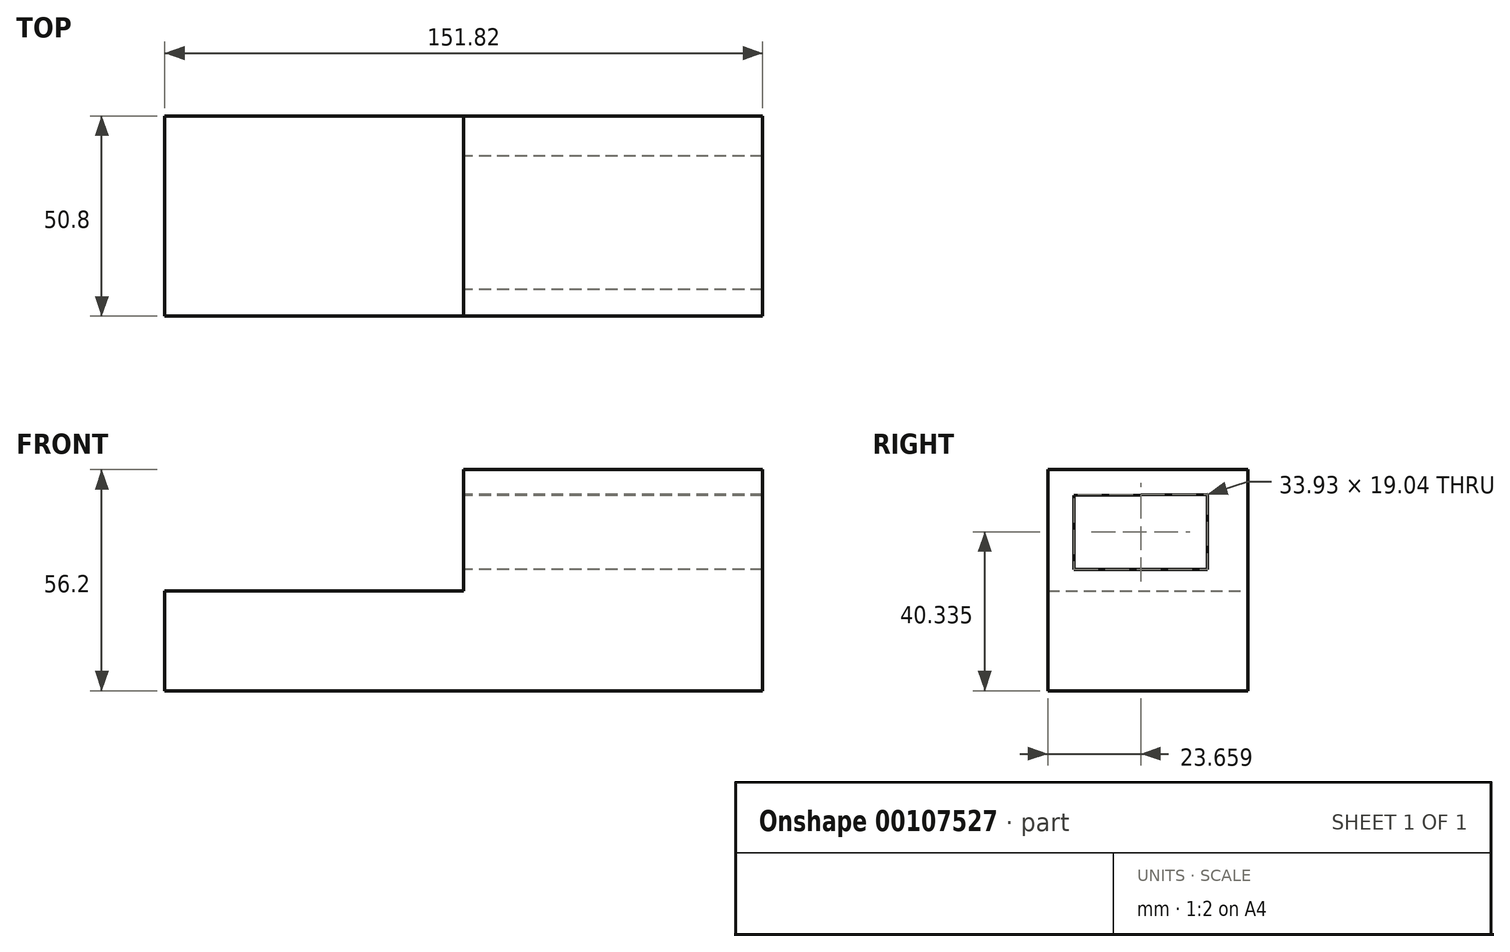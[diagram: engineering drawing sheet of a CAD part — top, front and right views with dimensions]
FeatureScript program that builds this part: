
annotation { "Feature Type Name" : "Feature", "Feature Type Description" : "" }
export const myFeature = defineFeature(function(context is Context, id is Id, definition is map)
    precondition{}
    {
        {
            var Q0;
            Q0=qCreatedBy(makeId("Front.planeOp"),FACE);
            var sketch = newSketch(context, id + "F0", { "sketchPlane" : qUnion([Q0])});
            skLineSegment(sketch, "E0", {"start": v(0, 56.2) * mm, "end": v(75.91, 56.2) * mm});
            skLineSegment(sketch, "E1", {"start": v(75.91, 56.2) * mm, "end": v(75.91, 0) * mm});
            skLineSegment(sketch, "E2", {"start": v(75.91, 0) * mm, "end": v(-75.91, 0) * mm});
            skLineSegment(sketch, "E3", {"start": v(-75.91, 0) * mm, "end": v(-75.91, 25.4) * mm});
            skLineSegment(sketch, "E4", {"start": v(-75.91, 25.4) * mm, "end": v(0, 25.4) * mm});
            skLineSegment(sketch, "E5", {"start": v(0, 25.4) * mm, "end": v(0, 56.2) * mm});
            skSolve(sketch);
        }
        {
            var Q0;
            Q0=makeQuery(id+"F0.imprint","IMPRINT",FACE,{"disambiguationData":[TD([[makeQuery(id+"F0.imprint","IMPRINT",EDGE,{"derivedFrom":sQuery(id+"F0.wireOp",EDGE,"E0")}),-1.0]])]});
            extrude(context, id + "F1", {"entities" : qUnion([Q0]), "depth" : 50.8 * mm});
        }
        {
            var Q0;
            Q0=qCreatedBy(makeId("Right.planeOp"),FACE);
            var sketch = newSketch(context, id + "F2", { "sketchPlane" : qUnion([Q0])});
            skLineSegment(sketch, "E6", {"start": v(-10.18, 49.85) * mm, "end": v(-10.18, 30.82) * mm});
            skLineSegment(sketch, "E7", {"start": v(-10.18, 30.82) * mm, "end": v(-44.1, 30.82) * mm});
            skLineSegment(sketch, "E8", {"start": v(-44.1, 30.82) * mm, "end": v(-44.1, 49.66) * mm});
            skLineSegment(sketch, "E9", {"start": v(-10.18, 49.85) * mm, "end": v(-44.1, 49.66) * mm});
            skLineSegment(sketch, "E10", {"start": v(-10.18, 56.07) * mm, "end": v(-10.18, 49.85) * mm});
            skLineSegment(sketch, "E11", {"start": v(-10.18, 30.82) * mm, "end": v(0, 30.82) * mm});
            skLineSegment(sketch, "E12", {"start": v(0, 30.82) * mm, "end": v(0, 0) * mm});
            skSolve(sketch);
        }
        {
            var Q0;
            Q0=makeQuery(id+"F2.imprint","IMPRINT",FACE,{"disambiguationData":[TD([[makeQuery(id+"F2.imprint","IMPRINT",EDGE,{"derivedFrom":sQuery(id+"F2.wireOp",EDGE,"E6")}),-1.0]])]});
            extrude(context, id + "F3", {"entities" : qUnion([Q0]), "operationType" : NewBodyOperationType.REMOVE, "depth" : 92.51 * mm});
        }
    });
